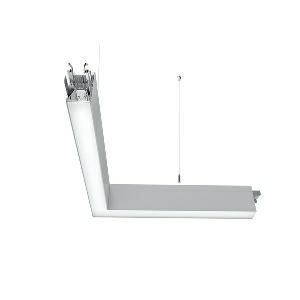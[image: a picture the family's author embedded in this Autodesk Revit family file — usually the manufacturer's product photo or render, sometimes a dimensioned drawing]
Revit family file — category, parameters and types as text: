
# Revit family: idoo_line_-_ilp_3000_830_d_lr_mid_00807707_2edc
name_source: partatom
category: Lighting Fixtures
units: mm (PartAtom-declared; Revit-internal decimal feet)

## family parameters
Cut with Voids When Loaded = No
Host = Face
Light Source = No
Part Type = Normal
Room Calculation Point = No
Round Connector Dimension = Use Diameter
Shared = No

## types (1)
- IDOO.line - ILP 3000/830/D/LR MID (1 x LED, 3000 lm, 3000K)
    Apparent Load = 23 VA
    Approval mark = CE
    CIE Flux Codes = 66 91 98 40 100
    Color Rendering = 80-89
    Color Temperature = 3000K
    Control Gear = Electronic ballast
    Default Elevation = 1800 mm
    Description = ILP 3000/830/D|Suspended luminaire|light source: LED|connected load: 220-240 V, 50/60 Hz|Power consumption: approx. 23 W|standby: approx. 0,20|luminous flux: 3000 lm|luminous efficacy: 130 lm/W|light distribution: Direct/indirect|direct ratio: approx. 40 %|colour temperature: Warm white, ca. 3000 K|color rendering index (CRI): >= 80|chromaticity tolerance:  3 SDCM|System of protection: IP 40|technology: Continuously dimmable|luminaire body|material: Sectional aluminium|colour: Silver|lamp cover: Acrylic (PMMA), Clear|Fastening: Steel cable 0.3 - 0.7 m|glare control: Prism aperture|luminance(L65): <= 2700 cd/m|unified glare rating(4H 8H): <=  16|special features: DALI Load 1x, TouchDIM - dimming via standard switch, Through-wired, up to 18 m on one mains connection, Flicker-free, Continous light without dark z, Suitable as emergency lighting, 90░ rerouting on the right sid, Mechanical and electrical connection of the individual modules without tools|
    Frequency = 50 Hz
    Height = 110 mm
    Lamp = 1 x LED
    Lamp Light Flux = 3000 lm
    Lamp count = 1
    Length = 600 mm
    Luminous efficacy = 130 lm/W
    Manufacturer = Waldmann
    ModVariant = No
    Model = 00807707
    Mounting Place = Ceiling
    Mounting Type = Pendant
    Number of Poles = 1
    OnlyDefault = Yes
    Power Factor = 1
    Product Name = IDOO.line - ILP 3000/830/D/LR MID
    Product group = Suspended luminaire
    ProductGroupID = 9
    Protection Class = Protection class I
    Protection Degree = IP 40
    RLX_Detail_Level = 1
    RLX_Emergency_Light_Flux = 0 lm
    RLX_Emergency_Type = 0
    RLX_Emergency_Type_DB = No
    RlxData = <blob elided: 21761 chars, md5=93036a85>
    Socket = socket
    Standby Power = 0 W
    System Light Flux = 3000 lm
    System Power = 23 W
    Type Comments = Product without accessories
    Type Image = ilp_dlp_lr_si.jpg
    URL = http://relux.com
    VarID = ---
    Voltage = 230 V
    Voltage Range = 220-240 V
    Weight = 0.00 kg
    Width = 600 mm

## geometry (parser evidence)
native form markers: Blend x4, Sweep x15
no freeform markers — native parametric forms only
